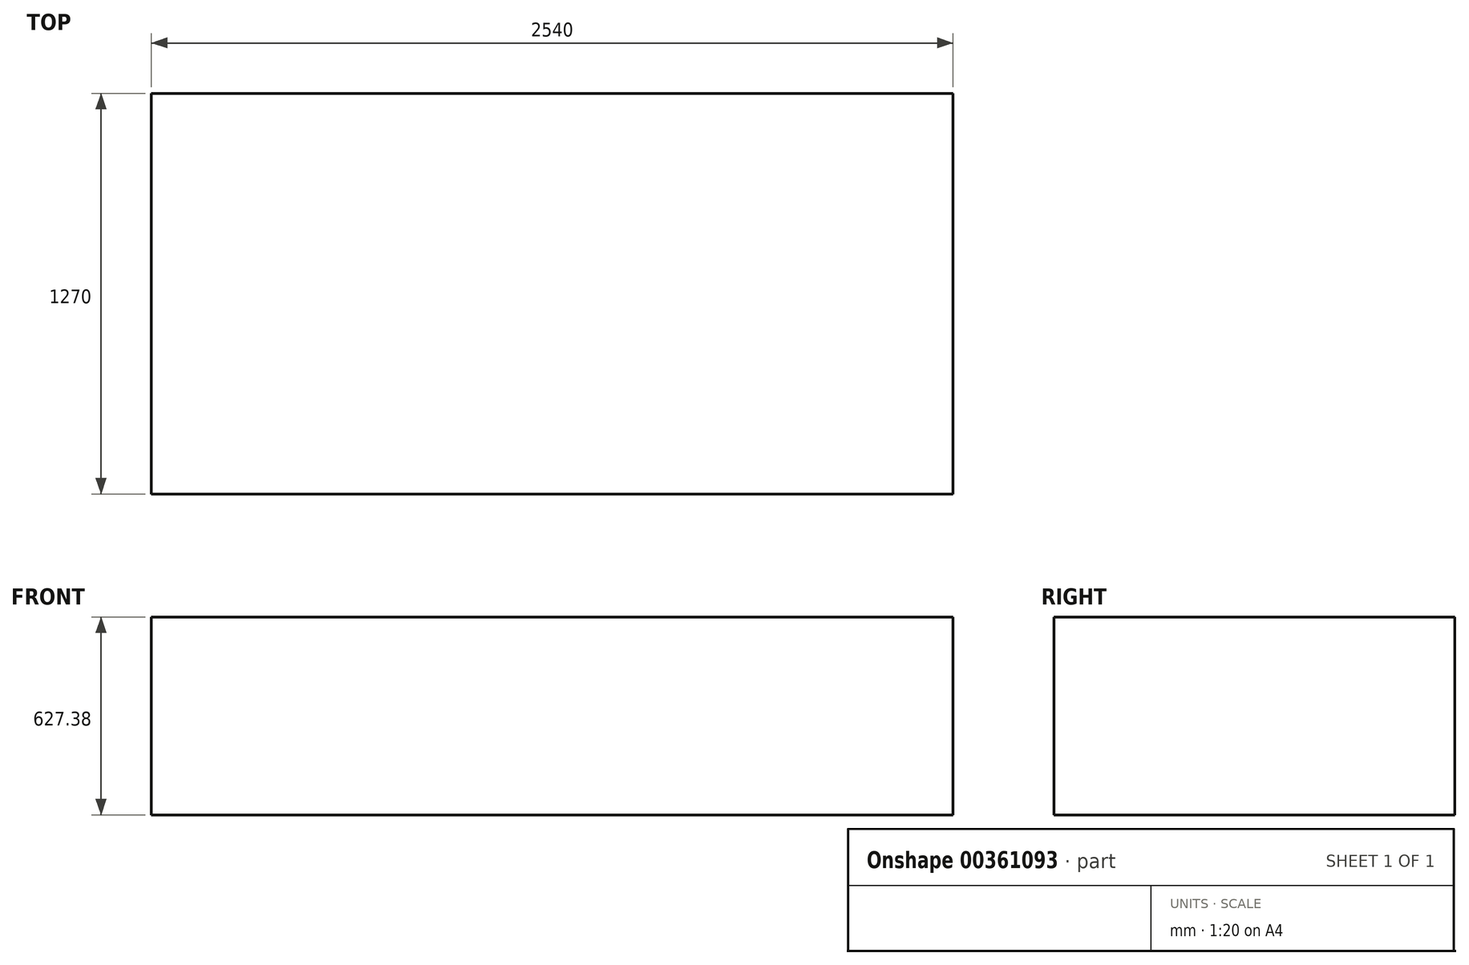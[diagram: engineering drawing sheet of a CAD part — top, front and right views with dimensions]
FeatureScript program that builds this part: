
annotation { "Feature Type Name" : "Feature", "Feature Type Description" : "" }
export const myFeature = defineFeature(function(context is Context, id is Id, definition is map)
    precondition{}
    {
        {
            var Q0;
            Q0=qCreatedBy(makeId("Top.planeOp"),FACE);
            var sketch = newSketch(context, id + "F0", { "sketchPlane" : qUnion([Q0])});
            skLineSegment(sketch, "E0.bottom", {"start": v(-1270, 4.8) * mm, "end": v(1270, 4.8) * mm});
            skLineSegment(sketch, "E0.top", {"start": v(-1270, -1265.2) * mm, "end": v(1270, -1265.2) * mm});
            skLineSegment(sketch, "E0.left", {"start": v(-1270, 4.8) * mm, "end": v(-1270, -1265.2) * mm});
            skLineSegment(sketch, "E0.right", {"start": v(1270, 4.8) * mm, "end": v(1270, -1265.2) * mm});
            skSolve(sketch);
        }
        {
            var Q0;
            Q0 = qSketchRegion(id + "F0", true);
            extrude(context, id + "F1", {"entities" : qUnion([Q0]), "depth" : 627.38 * mm});
        }
    });
